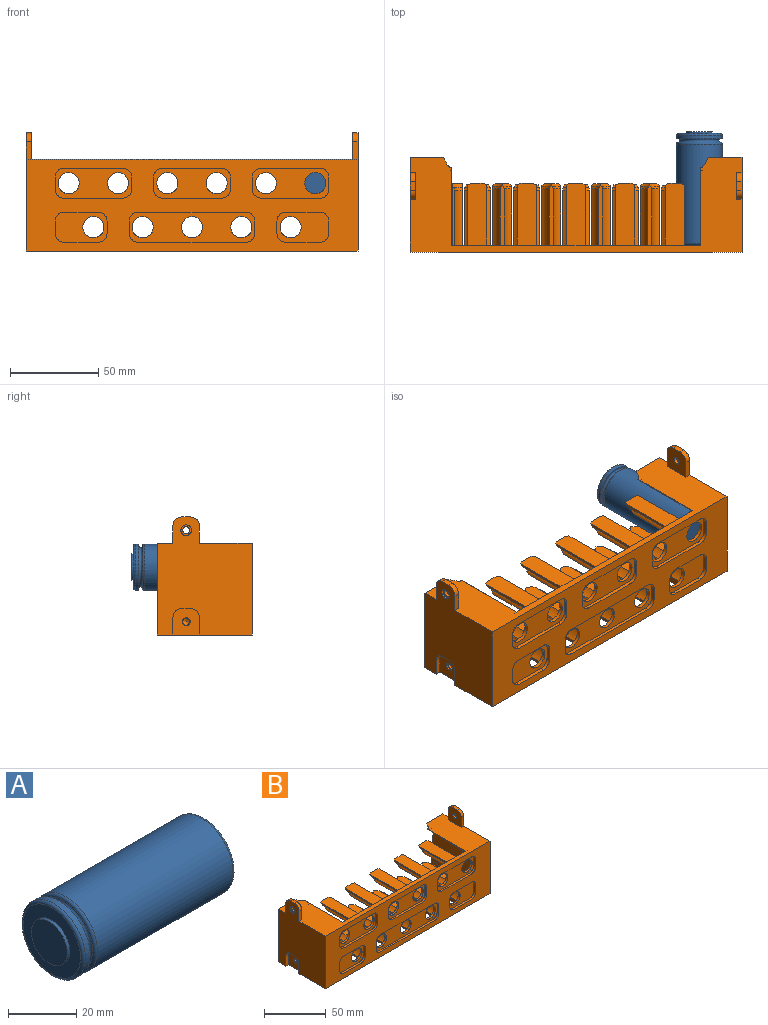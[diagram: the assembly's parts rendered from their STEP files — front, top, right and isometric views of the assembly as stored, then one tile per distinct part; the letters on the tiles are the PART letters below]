
ASSEMBLY  parts=2 mates=1
PART A: 11 faces, bbox 64.4x28.1x28.1 mm
  f0: torus R=11.97mm, axis (-1,0,0), area 223.8mm2, adj f1,f10
  f1: plane 25.95x25.95mm, normal (1,0,0), area 78.4mm2, adj f0,f2
  f2: cylinder r=12.97mm len=25.95mm, axis (-1,0,0), area 163mm2, adj f1,f3
  f3: torus R=11.97mm, axis (-1,0,0), area 124.5mm2, adj f2,f4
  f4: plane 23.95x23.95mm, normal (-1,0,0), area 273.8mm2, adj f3,f5
  f5: cylinder r=7.5mm len=15mm, axis (-1,0,0), area 47.1mm2, adj f4,f6
  f6: plane 15x15mm, normal (-1,0,0), area 176.7mm2, adj f5
  f7: plane 23.95x23.95mm, normal (1,0,0), area 450.5mm2, adj f8
  f8: torus R=11.97mm, axis (-1,0,0), area 124.5mm2, adj f7,f9
  f9: cylinder r=12.97mm len=56.4mm, axis (-1,0,0), area 4598mm2, adj f8,f10
  f10: torus R=11.97mm, axis (-1,0,0), area 124.5mm2, adj f0,f9
PART B: 320 faces, bbox 189.6x55.1x68.2 mm
  f0: plane 10x3mm, normal (0,-1,0), area 30mm2, adj f23,f29,f295,f310
  f1: plane 10x3mm, normal (0,1,0), area 30mm2, adj f23,f29,f295,f311
  f2: plane 10x3mm, normal (0,-1,0), area 30mm2, adj f4,f23,f28,f314
  f3: plane 10x3mm, normal (0,1,0), area 30mm2, adj f4,f23,f28,f315
  f4: plane 15x15mm, normal (1,0,0), area 198.4mm2, adj f2,f3,f23,f290,f306,f314,f315
  f5: plane 188.5x52mm, normal (0,-1,0), area 5493.8mm2, adj f23,f25,f28,f29,f234,f235,f236,f237
  f6: cylinder r=6mm len=12mm, axis (0,1,0), area 75.4mm2, adj f19,f251
  f7: cylinder r=6mm len=12mm, axis (0,1,0), area 75.4mm2, adj f19,f278
  f8: cylinder r=6mm len=12mm, axis (0,1,0), area 75.4mm2, adj f19,f278
  f9: cylinder r=6mm len=12mm, axis (0,1,0), area 75.4mm2, adj f19,f269
  f10: cylinder r=6mm len=12mm, axis (0,1,0), area 75.4mm2, adj f19,f260
  f11: cylinder r=6mm len=12mm, axis (0,1,0), area 75.4mm2, adj f19,f242
  f12: cylinder r=6mm len=12mm, axis (0,1,0), area 75.4mm2, adj f19,f260
  f13: cylinder r=6mm len=12mm, axis (0,1,0), area 75.4mm2, adj f19,f242
  f14: cylinder r=6mm len=12mm, axis (0,1,0), area 75.4mm2, adj f19,f251
  f15: cylinder r=6mm len=12mm, axis (0,1,0), area 75.4mm2, adj f19,f242
  f16: cylinder r=6mm len=12mm, axis (0,1,0), area 75.4mm2, adj f19,f233
  f17: plane 15x12mm, normal (1,0,0), area 180mm2, adj f23,f24,f149,f169
  f18: plane 7.81x4.31mm, normal (0,1,0), area 0.3mm2, adj f141,f145
  f19: plane 166.4x52mm, normal (0,1,0), area 6272.6mm2, adj f6,f7,f8,f9,f10,f11,f12,f13
  f20: plane 15x12mm, normal (-1,0,0), area 180mm2, adj f23,f130,f144,f168
  f21: cylinder r=13.2mm len=15mm, axis (0,-1,0), area 76.9mm2, adj f19,f139,f149,f150
  f22: plane 7.81x4.31mm, normal (0,1,0), area 0.3mm2, adj f139,f151
  f23: plane 188.5x54mm, normal (0,0,-1), area 3135.8mm2, adj f0,f1,f2,f3,f4,f5,f17,f19
  f24: plane 52.04x19.14mm, normal (0,1,0), area 594.4mm2, adj f17,f23,f25,f29,f125,f127,f149,f152
  f25: plane 188.5x54mm, normal (0,0,1), area 3000.9mm2, adj f5,f19,f24,f28,f29,f130,f140,f142
  f26: cone r=2mm half-angle=59deg, axis (0,1,0), area 14.7mm2, adj f27
  f27: cylinder r=2mm len=7.5mm, axis (0,1,0), area 94.2mm2, adj f26,f130
  f28: plane 67x54mm, normal (1,0,0), area 2779.7mm2, adj f2,f3,f5,f23,f25,f130,f287,f288
  f29: plane 67x54mm, normal (-1,0,0), area 2779.7mm2, adj f0,f1,f5,f23,f24,f25,f296,f297
  f30: plane 34.18x2.86mm, normal (-1,0,0), area 90mm2, adj f19,f47,f138,f216
  f31: cylinder r=13.2mm len=31.3mm, axis (0,-1,0), area 169.1mm2, adj f19,f32,f36,f218
  f32: plane 35.13x7.13mm, normal (0,0,1), area 234.3mm2, adj f19,f31,f33,f160,f206,f207,f218,f219
  f33: cylinder r=13.2mm len=31.3mm, axis (0,-1,0), area 169.1mm2, adj f19,f32,f34,f219
  f34: plane 34.35x1.97mm, normal (0.87,0,-0.49), area 74.6mm2, adj f19,f33,f35,f207,f219
  f35: cylinder r=13.2mm len=35mm, axis (0,-1,0), area 469.7mm2, adj f19,f34,f36,f160,f206,f207
  f36: plane 34.35x1.97mm, normal (-0.87,0,-0.49), area 74.6mm2, adj f19,f31,f35,f206,f218
  f37: cylinder r=13.2mm len=32.05mm, axis (0,-1,0), area 266.7mm2, adj f19,f38,f42,f197
  f38: plane 34.03x1.51mm, normal (-1,0,0), area 49.8mm2, adj f19,f37,f39,f171,f197
  f39: plane 35.05x10.82mm, normal (0,0,1), area 375.3mm2, adj f19,f38,f40,f164,f170,f171
  f40: plane 34.03x1.51mm, normal (1,0,0), area 49.8mm2, adj f19,f39,f41,f170,f196
  f41: cylinder r=13.2mm len=32.05mm, axis (0,-1,0), area 266.7mm2, adj f19,f40,f42,f196
  f42: plane 33.97x2.29mm, normal (0,0,-1), area 76.1mm2, adj f19,f37,f41,f170,f171,f196,f197
  f43: plane 34.03x1.51mm, normal (-1,0,0), area 49.8mm2, adj f19,f44,f46,f182,f202
  f44: cylinder r=13.2mm len=32.05mm, axis (0,-1,0), area 266.7mm2, adj f19,f43,f45,f202
  f45: plane 33.97x2.29mm, normal (0,0,1), area 76.1mm2, adj f19,f44,f66,f182,f183,f202,f203
  f46: plane 35.05x10.82mm, normal (0,0,-1), area 375.3mm2, adj f19,f43,f67,f157,f182,f183
  f47: plane 33.22x1.15mm, normal (0,0,1), area 37.2mm2, adj f19,f30,f48,f216,f228
  f48: cylinder r=13.2mm len=31.3mm, axis (0,-1,0), area 260.4mm2, adj f19,f47,f49,f228
  f49: plane 35.05x3.64mm, normal (1,0,0), area 116.9mm2, adj f19,f23,f48,f216,f228
  f50: cylinder r=13.2mm len=31.3mm, axis (0,-1,0), area 169.1mm2, adj f19,f51,f55,f220
  f51: plane 35.13x7.13mm, normal (0,0,1), area 234.3mm2, adj f19,f50,f52,f162,f208,f209,f220,f221
  f52: cylinder r=13.2mm len=31.3mm, axis (0,-1,0), area 169.1mm2, adj f19,f51,f53,f221
  f53: plane 34.35x1.97mm, normal (0.87,0,-0.49), area 74.6mm2, adj f19,f52,f54,f209,f221
  f54: cylinder r=13.2mm len=35mm, axis (0,-1,0), area 469.7mm2, adj f19,f53,f55,f162,f208,f209
  f55: plane 34.35x1.97mm, normal (-0.87,0,-0.49), area 74.6mm2, adj f19,f50,f54,f208,f220
  f56: cylinder r=13.2mm len=32.05mm, axis (0,-1,0), area 266.7mm2, adj f19,f57,f61,f195
  f57: plane 34.03x1.51mm, normal (-1,0,0), area 49.8mm2, adj f19,f56,f58,f173,f195
  f58: plane 35.05x10.82mm, normal (0,0,1), area 375.3mm2, adj f19,f57,f59,f167,f172,f173
  f59: plane 34.03x1.51mm, normal (1,0,0), area 49.8mm2, adj f19,f58,f60,f172,f194
  f60: cylinder r=13.2mm len=32.05mm, axis (0,-1,0), area 266.7mm2, adj f19,f59,f61,f194
  f61: plane 33.97x2.29mm, normal (0,0,-1), area 76.1mm2, adj f19,f56,f60,f172,f173,f194,f195
  f62: plane 34.03x1.51mm, normal (-1,0,0), area 49.8mm2, adj f19,f63,f65,f186,f205
  f63: cylinder r=13.2mm len=32.05mm, axis (0,-1,0), area 266.7mm2, adj f19,f62,f64,f205
  f64: plane 33.97x2.29mm, normal (0,0,1), area 76.1mm2, adj f19,f63,f84,f186,f187,f204,f205
  f65: plane 35.05x10.82mm, normal (0,0,-1), area 375.3mm2, adj f19,f62,f85,f156,f186,f187
  f66: cylinder r=13.2mm len=32.05mm, axis (0,-1,0), area 266.7mm2, adj f19,f45,f67,f203
  f67: plane 34.03x1.51mm, normal (1,0,0), area 49.8mm2, adj f19,f46,f66,f183,f203
  f68: cylinder r=13.2mm len=31.3mm, axis (0,-1,0), area 169.1mm2, adj f19,f69,f73,f222
  f69: plane 35.13x7.13mm, normal (0,0,1), area 234.3mm2, adj f19,f68,f70,f161,f210,f211,f222,f223
  f70: cylinder r=13.2mm len=31.3mm, axis (0,-1,0), area 169.1mm2, adj f19,f69,f71,f223
  f71: plane 34.35x1.97mm, normal (0.87,0,-0.49), area 74.6mm2, adj f19,f70,f72,f211,f223
  f72: cylinder r=13.2mm len=35mm, axis (0,-1,0), area 469.7mm2, adj f19,f71,f73,f161,f210,f211
  f73: plane 34.35x1.97mm, normal (-0.87,0,-0.49), area 74.6mm2, adj f19,f68,f72,f210,f222
  f74: cylinder r=13.2mm len=32.05mm, axis (0,-1,0), area 266.7mm2, adj f19,f75,f79,f193
  f75: plane 34.03x1.51mm, normal (-1,0,0), area 49.8mm2, adj f19,f74,f76,f175,f193
  f76: plane 35.05x10.82mm, normal (0,0,1), area 375.3mm2, adj f19,f75,f77,f166,f174,f175
  f77: plane 34.03x1.51mm, normal (1,0,0), area 49.8mm2, adj f19,f76,f78,f174,f192
  f78: cylinder r=13.2mm len=32.05mm, axis (0,-1,0), area 266.7mm2, adj f19,f77,f79,f192
  f79: plane 33.97x2.29mm, normal (0,0,-1), area 76.1mm2, adj f19,f74,f78,f174,f175,f192,f193
  f80: plane 34.03x1.51mm, normal (-1,0,0), area 49.8mm2, adj f19,f81,f83,f184,f201
  f81: cylinder r=13.2mm len=32.05mm, axis (0,-1,0), area 266.7mm2, adj f19,f80,f82,f201
  f82: plane 33.97x2.29mm, normal (0,0,1), area 76.1mm2, adj f19,f81,f102,f184,f185,f199,f201
  f83: plane 35.05x10.82mm, normal (0,0,-1), area 375.3mm2, adj f19,f80,f103,f155,f184,f185
  f84: cylinder r=13.2mm len=32.05mm, axis (0,-1,0), area 266.7mm2, adj f19,f64,f85,f204
  f85: plane 34.03x1.51mm, normal (1,0,0), area 49.8mm2, adj f19,f65,f84,f187,f204
  f86: cylinder r=13.2mm len=31.3mm, axis (0,-1,0), area 169.1mm2, adj f19,f87,f91,f224
  f87: plane 35.13x7.13mm, normal (0,0,1), area 234.3mm2, adj f19,f86,f88,f159,f212,f213,f224,f225
  f88: cylinder r=13.2mm len=31.3mm, axis (0,-1,0), area 169.1mm2, adj f19,f87,f89,f225
  f89: plane 34.35x1.97mm, normal (0.87,0,-0.49), area 74.6mm2, adj f19,f88,f90,f213,f225
  f90: cylinder r=13.2mm len=35mm, axis (0,-1,0), area 469.7mm2, adj f19,f89,f91,f159,f212,f213
  f91: plane 34.35x1.97mm, normal (-0.87,0,-0.49), area 74.6mm2, adj f19,f86,f90,f212,f224
  f92: cylinder r=13.2mm len=32.05mm, axis (0,-1,0), area 266.7mm2, adj f19,f93,f97,f191
  f93: plane 34.03x1.51mm, normal (-1,0,0), area 49.8mm2, adj f19,f92,f94,f177,f191
  f94: plane 35.05x10.82mm, normal (0,0,1), area 375.3mm2, adj f19,f93,f95,f165,f176,f177
  f95: plane 34.03x1.51mm, normal (1,0,0), area 49.8mm2, adj f19,f94,f96,f176,f190
  f96: cylinder r=13.2mm len=32.05mm, axis (0,-1,0), area 266.7mm2, adj f19,f95,f97,f190
  f97: plane 33.97x2.29mm, normal (0,0,-1), area 76.1mm2, adj f19,f92,f96,f176,f177,f190,f191
  f98: plane 34.03x1.51mm, normal (-1,0,0), area 49.8mm2, adj f19,f99,f101,f180,f200
  f99: cylinder r=13.2mm len=32.05mm, axis (0,-1,0), area 266.7mm2, adj f19,f98,f100,f200
  f100: plane 33.97x2.29mm, normal (0,0,1), area 76.1mm2, adj f19,f99,f120,f180,f181,f198,f200
  f101: plane 35.05x10.82mm, normal (0,0,-1), area 375.3mm2, adj f19,f98,f121,f154,f180,f181
  f102: cylinder r=13.2mm len=32.05mm, axis (0,-1,0), area 266.7mm2, adj f19,f82,f103,f199
  f103: plane 34.03x1.51mm, normal (1,0,0), area 49.8mm2, adj f19,f83,f102,f185,f199
  f104: plane 34.18x2.86mm, normal (1,0,0), area 90mm2, adj f19,f119,f137,f217
  f105: cylinder r=13.2mm len=31.3mm, axis (0,-1,0), area 169.1mm2, adj f19,f106,f110,f226
  f106: plane 35.13x7.13mm, normal (0,0,1), area 234.3mm2, adj f19,f105,f107,f158,f214,f215,f226,f227
  f107: cylinder r=13.2mm len=31.3mm, axis (0,-1,0), area 169.1mm2, adj f19,f106,f108,f227
  f108: plane 33.64x1.97mm, normal (0.87,0,-0.49), area 74.1mm2, adj f19,f107,f109,f214,f227,f230,f232
  f109: cylinder r=13.2mm len=32.58mm, axis (0,-1,0), area 439.1mm2, adj f19,f108,f110,f232
  f110: plane 33.64x1.97mm, normal (-0.87,0,-0.49), area 74.1mm2, adj f19,f105,f109,f215,f226,f231,f232
  f111: cylinder r=13.2mm len=32.05mm, axis (0,-1,0), area 266.7mm2, adj f19,f112,f116,f189
  f112: plane 34.03x1.51mm, normal (-1,0,0), area 49.8mm2, adj f19,f111,f113,f179,f189
  f113: plane 35.05x10.82mm, normal (0,0,1), area 375.3mm2, adj f19,f112,f114,f163,f178,f179
  f114: plane 34.03x1.51mm, normal (1,0,0), area 49.8mm2, adj f19,f113,f115,f178,f188
  f115: cylinder r=13.2mm len=32.05mm, axis (0,-1,0), area 266.7mm2, adj f19,f114,f116,f188
  f116: plane 33.97x2.29mm, normal (0,0,-1), area 76.1mm2, adj f19,f111,f115,f178,f179,f188,f189
  f117: plane 35.05x3.64mm, normal (-1,0,0), area 116.9mm2, adj f19,f23,f118,f217,f229
  f118: cylinder r=13.2mm len=31.3mm, axis (0,-1,0), area 260.4mm2, adj f19,f117,f119,f229
  f119: plane 33.22x1.15mm, normal (0,0,1), area 37.2mm2, adj f19,f104,f118,f217,f229
  f120: cylinder r=13.2mm len=32.05mm, axis (0,-1,0), area 266.7mm2, adj f19,f100,f121,f198
  f121: plane 34.03x1.51mm, normal (1,0,0), area 49.8mm2, adj f19,f101,f120,f181,f198
  f122: cone r=3.52mm half-angle=59deg, axis (0,1,0), area 45.5mm2, adj f123
  f123: cylinder r=3.52mm len=7.05mm, axis (0,1,0), area 135.1mm2, adj f122,f124
  f124: plane 7.5x7.5mm, normal (0,1,0), area 5.1mm2, adj f123,f125
  f125: cylinder r=3.75mm len=7.5mm, axis (0,1,0), area 23.6mm2, adj f24,f124
  f126: cone r=2mm half-angle=59deg, axis (0,1,0), area 14.7mm2, adj f127
  f127: cylinder r=2mm len=7.5mm, axis (0,1,0), area 94.2mm2, adj f24,f126
  f128: cylinder r=13.2mm len=15mm, axis (0,-1,0), area 76.9mm2, adj f19,f129,f141,f144
  f129: cone r=13.2mm half-angle=8deg, axis (0,1,0), area 0mm2, adj f128,f143,f146
  f130: plane 52.03x19.14mm, normal (0,1,0), area 594.4mm2, adj f20,f23,f25,f27,f28,f134,f144,f147
  f131: cone r=3.52mm half-angle=59deg, axis (0,1,0), area 45.5mm2, adj f132
  f132: cylinder r=3.52mm len=7.05mm, axis (0,1,0), area 135.1mm2, adj f131,f133
  f133: plane 7.5x7.5mm, normal (0,1,0), area 5.1mm2, adj f132,f134
  f134: cylinder r=3.75mm len=7.5mm, axis (0,1,0), area 23.6mm2, adj f130,f133
  f135: extruded ~35x7.31mm, area 306.1mm2, adj f19,f137,f144,f168
  f136: extruded ~35x7.31mm, area 306.1mm2, adj f19,f138,f149,f169
  f137: cylinder r=4mm len=35mm, axis (0,-1,0), area 313mm2, adj f19,f104,f135,f168,f217
  f138: cylinder r=4mm len=35mm, axis (0,-1,0), area 313mm2, adj f19,f30,f136,f169,f216
  f139: cylinder r=12.55mm len=15mm, axis (0,-1,0), area 226.5mm2, adj f19,f21,f22,f140,f150,f151
  f140: plane 43.78x0.46mm, normal (1,0,0), area 19mm2, adj f19,f25,f139,f151,f152,f153
  f141: cylinder r=12.55mm len=15mm, axis (0,-1,0), area 226.5mm2, adj f18,f19,f128,f142,f145,f146
  f142: plane 43.78x0.46mm, normal (-1,0,0), area 19mm2, adj f19,f25,f141,f145,f147,f148
  f143: plane 0x0mm, normal (0,0,-1), area 0mm2, adj f129
  f144: plane 51.1x32.4mm, normal (-1,0,0.08), area 1361.7mm2, adj f19,f20,f128,f130,f135,f145,f147,f148
  f145: extruded ~22x13.04mm, area 445.3mm2, adj f18,f141,f142,f144,f146,f148
  f146: plane 9.03x3.52mm, normal (0,-1,0), area 0.1mm2, adj f129,f141,f145
  f147: bspline ~13.9x13.28mm, area 122.4mm2, adj f25,f130,f142,f144,f148
  f148: bspline ~13.32x13mm, area 102.5mm2, adj f142,f144,f145,f147
  f149: plane 51.1x32.4mm, normal (1,0,0.08), area 1361.7mm2, adj f17,f19,f21,f24,f136,f151,f152,f153
  f150: plane 9.04x3.52mm, normal (0,-1,0), area 0.1mm2, adj f21,f139,f151
  f151: extruded ~22x13.04mm, area 445.3mm2, adj f22,f139,f140,f149,f150,f153
  f152: bspline ~13.9x13.28mm, area 122.4mm2, adj f24,f25,f140,f149,f153
  f153: bspline ~13.31x12.98mm, area 102.5mm2, adj f140,f149,f151,f152
  f154: plane 7.67x5.21mm, normal (0,1,0), area 17mm2, adj f101,f180,f181
  f155: plane 7.67x5.21mm, normal (0,1,0), area 17mm2, adj f83,f184,f185
  f156: plane 7.67x5.21mm, normal (0,1,0), area 17mm2, adj f65,f186,f187
  f157: plane 7.67x5.21mm, normal (0,1,0), area 17mm2, adj f46,f182,f183
  f158: plane 4.44x2.97mm, normal (0,1,0), area 5.6mm2, adj f106,f214,f215,f232
  f159: plane 7.24x4.31mm, normal (0,1,0), area 11.4mm2, adj f87,f90,f212,f213
  f160: plane 7.24x4.31mm, normal (0,1,0), area 11.4mm2, adj f32,f35,f206,f207
  f161: plane 7.24x4.31mm, normal (0,1,0), area 11.4mm2, adj f69,f72,f210,f211
  f162: plane 7.24x4.31mm, normal (0,1,0), area 11.4mm2, adj f51,f54,f208,f209
  f163: plane 7.67x5.21mm, normal (0,1,0), area 17mm2, adj f113,f178,f179
  f164: plane 7.67x5.21mm, normal (0,1,0), area 17mm2, adj f39,f170,f171
  f165: plane 7.67x5.21mm, normal (0,1,0), area 17mm2, adj f94,f176,f177
  f166: plane 7.67x5.21mm, normal (0,1,0), area 17mm2, adj f76,f174,f175
  f167: plane 7.67x5.21mm, normal (0,1,0), area 17mm2, adj f58,f172,f173
  f168: plane 16.23x12mm, normal (0,1,0), area 74.4mm2, adj f20,f23,f135,f137,f217
  f169: plane 16.23x12mm, normal (0,1,0), area 74.4mm2, adj f17,f23,f136,f138,f216
  f170: cone r=15.35mm half-angle=45deg, axis (0,1,0), area 20mm2, adj f39,f40,f42,f164,f171,f196
  f171: cone r=15.35mm half-angle=45deg, axis (0,1,0), area 20mm2, adj f38,f39,f42,f164,f170,f197
  f172: cone r=15.35mm half-angle=45deg, axis (0,1,0), area 20mm2, adj f58,f59,f61,f167,f173,f194
  f173: cone r=15.35mm half-angle=45deg, axis (0,1,0), area 20mm2, adj f57,f58,f61,f167,f172,f195
  f174: cone r=15.35mm half-angle=45deg, axis (0,1,0), area 20mm2, adj f76,f77,f79,f166,f175,f192
  f175: cone r=15.35mm half-angle=45deg, axis (0,1,0), area 20mm2, adj f75,f76,f79,f166,f174,f193
  f176: cone r=15.35mm half-angle=45deg, axis (0,1,0), area 20mm2, adj f94,f95,f97,f165,f177,f190
  f177: cone r=15.35mm half-angle=45deg, axis (0,1,0), area 20mm2, adj f93,f94,f97,f165,f176,f191
  f178: cone r=15.35mm half-angle=45deg, axis (0,1,0), area 20mm2, adj f113,f114,f116,f163,f179,f188
  f179: cone r=15.35mm half-angle=45deg, axis (0,1,0), area 20mm2, adj f112,f113,f116,f163,f178,f189
  f180: cone r=15.35mm half-angle=45deg, axis (0,1,0), area 20mm2, adj f98,f100,f101,f154,f181,f200
  f181: cone r=15.35mm half-angle=45deg, axis (0,1,0), area 20mm2, adj f100,f101,f121,f154,f180,f198
  f182: cone r=15.35mm half-angle=45deg, axis (0,1,0), area 20mm2, adj f43,f45,f46,f157,f183,f202
  f183: cone r=15.35mm half-angle=45deg, axis (0,1,0), area 20mm2, adj f45,f46,f67,f157,f182,f203
  f184: cone r=15.35mm half-angle=45deg, axis (0,1,0), area 20mm2, adj f80,f82,f83,f155,f185,f201
  f185: cone r=15.35mm half-angle=45deg, axis (0,1,0), area 20mm2, adj f82,f83,f103,f155,f184,f199
  f186: cone r=15.35mm half-angle=45deg, axis (0,1,0), area 20mm2, adj f62,f64,f65,f156,f187,f205
  f187: cone r=15.35mm half-angle=45deg, axis (0,1,0), area 20mm2, adj f64,f65,f85,f156,f186,f204
  f188: cone r=13.2mm half-angle=22.5deg, axis (0,1,0), area 13mm2, adj f114,f115,f116,f178
  f189: cone r=13.2mm half-angle=22.5deg, axis (0,1,0), area 13mm2, adj f111,f112,f116,f179
  f190: cone r=13.2mm half-angle=22.5deg, axis (0,1,0), area 13mm2, adj f95,f96,f97,f176
  f191: cone r=13.2mm half-angle=22.5deg, axis (0,1,0), area 13mm2, adj f92,f93,f97,f177
  f192: cone r=13.2mm half-angle=22.5deg, axis (0,1,0), area 13mm2, adj f77,f78,f79,f174
  f193: cone r=13.2mm half-angle=22.5deg, axis (0,1,0), area 13mm2, adj f74,f75,f79,f175
  f194: cone r=13.2mm half-angle=22.5deg, axis (0,1,0), area 13mm2, adj f59,f60,f61,f172
  f195: cone r=13.2mm half-angle=22.5deg, axis (0,1,0), area 13mm2, adj f56,f57,f61,f173
  f196: cone r=13.2mm half-angle=22.5deg, axis (0,1,0), area 13mm2, adj f40,f41,f42,f170
  f197: cone r=13.2mm half-angle=22.5deg, axis (0,1,0), area 13mm2, adj f37,f38,f42,f171
  f198: cone r=13.2mm half-angle=22.5deg, axis (0,1,0), area 13mm2, adj f100,f120,f121,f181
  f199: cone r=13.2mm half-angle=22.5deg, axis (0,1,0), area 13mm2, adj f82,f102,f103,f185
  f200: cone r=13.2mm half-angle=22.5deg, axis (0,1,0), area 13mm2, adj f98,f99,f100,f180
  f201: cone r=13.2mm half-angle=22.5deg, axis (0,1,0), area 13mm2, adj f80,f81,f82,f184
  f202: cone r=13.2mm half-angle=22.5deg, axis (0,1,0), area 13mm2, adj f43,f44,f45,f182
  f203: cone r=13.2mm half-angle=22.5deg, axis (0,1,0), area 13mm2, adj f45,f66,f67,f183
  f204: cone r=13.2mm half-angle=22.5deg, axis (0,1,0), area 13mm2, adj f64,f84,f85,f187
  f205: cone r=13.2mm half-angle=22.5deg, axis (0,1,0), area 13mm2, adj f62,f63,f64,f186
  f206: cone r=16.1mm half-angle=45deg, axis (0,1,0), area 22.8mm2, adj f32,f35,f36,f160,f218
  f207: cone r=16.1mm half-angle=45deg, axis (0,1,0), area 22.8mm2, adj f32,f34,f35,f160,f219
  f208: cone r=16.1mm half-angle=45deg, axis (0,1,0), area 22.8mm2, adj f51,f54,f55,f162,f220
  f209: cone r=16.1mm half-angle=45deg, axis (0,1,0), area 22.8mm2, adj f51,f53,f54,f162,f221
  f210: cone r=16.1mm half-angle=45deg, axis (0,1,0), area 22.8mm2, adj f69,f72,f73,f161,f222
  f211: cone r=16.1mm half-angle=45deg, axis (0,1,0), area 22.8mm2, adj f69,f71,f72,f161,f223
  f212: cone r=16.1mm half-angle=45deg, axis (0,1,0), area 22.8mm2, adj f87,f90,f91,f159,f224
  f213: cone r=16.1mm half-angle=45deg, axis (0,1,0), area 22.8mm2, adj f87,f89,f90,f159,f225
  f214: cone r=16.1mm half-angle=45deg, axis (0,1,0), area 18.8mm2, adj f106,f108,f158,f227,f230,f232
  f215: cone r=16.1mm half-angle=45deg, axis (0,1,0), area 18.8mm2, adj f106,f110,f158,f226,f231,f232
  f216: cone r=16.1mm half-angle=45deg, axis (0,1,0), area 30.1mm2, adj f23,f30,f47,f49,f138,f169,f228
  f217: cone r=16.1mm half-angle=45deg, axis (0,1,0), area 30.1mm2, adj f23,f104,f117,f119,f137,f168,f229
  f218: cone r=13.2mm half-angle=22.5deg, axis (0,1,0), area 8.5mm2, adj f31,f32,f36,f206
  f219: cone r=13.2mm half-angle=22.5deg, axis (0,1,0), area 8.5mm2, adj f32,f33,f34,f207
  f220: cone r=13.2mm half-angle=22.5deg, axis (0,1,0), area 8.5mm2, adj f50,f51,f55,f208
  f221: cone r=13.2mm half-angle=22.5deg, axis (0,1,0), area 8.5mm2, adj f51,f52,f53,f209
  f222: cone r=13.2mm half-angle=22.5deg, axis (0,1,0), area 8.5mm2, adj f68,f69,f73,f210
  f223: cone r=13.2mm half-angle=22.5deg, axis (0,1,0), area 8.5mm2, adj f69,f70,f71,f211
  f224: cone r=13.2mm half-angle=22.5deg, axis (0,1,0), area 8.5mm2, adj f86,f87,f91,f212
  f225: cone r=13.2mm half-angle=22.5deg, axis (0,1,0), area 8.5mm2, adj f87,f88,f89,f213
  f226: cone r=13.2mm half-angle=22.5deg, axis (0,1,0), area 8.5mm2, adj f105,f106,f110,f215
  f227: cone r=13.2mm half-angle=22.5deg, axis (0,1,0), area 8.5mm2, adj f106,f107,f108,f214
  f228: cone r=13.2mm half-angle=22.5deg, axis (0,1,0), area 13mm2, adj f47,f48,f49,f216
  f229: cone r=13.2mm half-angle=22.5deg, axis (0,1,0), area 13mm2, adj f117,f118,f119,f217
  f230: bspline ~4.87x2.24mm, area 0.5mm2, adj f108,f214,f232
  f231: bspline ~2.84x1.42mm, area 0.5mm2, adj f110,f215,f232
  f232: cone r=13.2mm half-angle=22.5deg, axis (0,1,0), area 27.8mm2, adj f108,f109,f110,f158,f214,f215,f230,f231
  f233: plane 29.5x17mm, normal (0,-1,0), area 366.9mm2, adj f16,f234,f235,f236,f237,f238,f239,f240
  f234: plane 7x2mm, normal (1,0,0), area 14mm2, adj f5,f233,f235,f241
  f235: cylinder r=5mm len=5mm, axis (0,-1,0), area 15.7mm2, adj f5,f233,f234,f236
  f236: plane 19.5x2mm, normal (0,0,1), area 39mm2, adj f5,f233,f235,f237
  f237: cylinder r=5mm len=5mm, axis (0,-1,0), area 15.7mm2, adj f5,f233,f236,f238
  f238: plane 7x2mm, normal (-1,0,0), area 14mm2, adj f5,f233,f237,f239
  f239: cylinder r=5mm len=5mm, axis (0,-1,0), area 15.7mm2, adj f5,f233,f238,f240
  f240: plane 19.5x2mm, normal (0,0,-1), area 39mm2, adj f5,f233,f239,f241
  f241: cylinder r=5mm len=5mm, axis (0,-1,0), area 15.7mm2, adj f5,f233,f234,f240
  f242: plane 71.5x17mm, normal (0,-1,0), area 854.7mm2, adj f11,f13,f15,f243,f244,f245,f246,f247
  f243: plane 61.5x2mm, normal (0,0,-1), area 123mm2, adj f5,f242,f244,f250
  f244: cylinder r=5mm len=5mm, axis (0,-1,0), area 15.7mm2, adj f5,f242,f243,f245
  f245: plane 7x2mm, normal (1,0,0), area 14mm2, adj f5,f242,f244,f246
  f246: cylinder r=5mm len=5mm, axis (0,-1,0), area 15.7mm2, adj f5,f242,f245,f247
  f247: plane 61.5x2mm, normal (0,0,1), area 123mm2, adj f5,f242,f246,f248
  f248: cylinder r=5mm len=5mm, axis (0,-1,0), area 15.7mm2, adj f5,f242,f247,f249
  f249: plane 7x2mm, normal (-1,0,0), area 14mm2, adj f5,f242,f248,f250
  f250: cylinder r=5mm len=5mm, axis (0,-1,0), area 15.7mm2, adj f5,f242,f243,f249
  f251: plane 43.5x17mm, normal (0,-1,0), area 491.8mm2, adj f6,f14,f252,f253,f254,f255,f256,f257
  f252: plane 7x2mm, normal (-1,0,0), area 14mm2, adj f5,f251,f253,f259
  f253: cylinder r=5mm len=5mm, axis (0,-1,0), area 15.7mm2, adj f5,f251,f252,f254
  f254: plane 33.5x2mm, normal (0,0,-1), area 67mm2, adj f5,f251,f253,f255
  f255: cylinder r=5mm len=5mm, axis (0,-1,0), area 15.7mm2, adj f5,f251,f254,f256
  f256: plane 7x2mm, normal (1,0,0), area 14mm2, adj f5,f251,f255,f257
  f257: cylinder r=5mm len=5mm, axis (0,-1,0), area 15.7mm2, adj f5,f251,f256,f258
  f258: plane 33.5x2mm, normal (0,0,1), area 67mm2, adj f5,f251,f257,f259
  f259: cylinder r=5mm len=5mm, axis (0,-1,0), area 15.7mm2, adj f5,f251,f252,f258
  f260: plane 43.5x17mm, normal (0,-1,0), area 491.8mm2, adj f10,f12,f261,f262,f263,f264,f265,f266
  f261: plane 33.5x2mm, normal (0,0,-1), area 67mm2, adj f5,f260,f262,f268
  f262: cylinder r=5mm len=5mm, axis (0,-1,0), area 15.7mm2, adj f5,f260,f261,f263
  f263: plane 7x2mm, normal (1,0,0), area 14mm2, adj f5,f260,f262,f264
  f264: cylinder r=5mm len=5mm, axis (0,-1,0), area 15.7mm2, adj f5,f260,f263,f265
  f265: plane 33.5x2mm, normal (0,0,1), area 67mm2, adj f5,f260,f264,f266
  f266: cylinder r=5mm len=5mm, axis (0,-1,0), area 15.7mm2, adj f5,f260,f265,f267
  f267: plane 7x2mm, normal (-1,0,0), area 14mm2, adj f5,f260,f266,f268
  f268: cylinder r=5mm len=5mm, axis (0,-1,0), area 15.7mm2, adj f5,f260,f261,f267
  f269: plane 29.5x17mm, normal (0,-1,0), area 366.9mm2, adj f9,f270,f271,f272,f273,f274,f275,f276
  f270: plane 7x2mm, normal (-1,0,0), area 14mm2, adj f5,f269,f271,f277
  f271: cylinder r=5mm len=5mm, axis (0,-1,0), area 15.7mm2, adj f5,f269,f270,f272
  f272: plane 19.5x2mm, normal (0,0,-1), area 39mm2, adj f5,f269,f271,f273
  f273: cylinder r=5mm len=5mm, axis (0,-1,0), area 15.7mm2, adj f5,f269,f272,f274
  f274: plane 7x2mm, normal (1,0,0), area 14mm2, adj f5,f269,f273,f275
  f275: cylinder r=5mm len=5mm, axis (0,-1,0), area 15.7mm2, adj f5,f269,f274,f276
  f276: plane 19.5x2mm, normal (0,0,1), area 39mm2, adj f5,f269,f275,f277
  f277: cylinder r=5mm len=5mm, axis (0,-1,0), area 15.7mm2, adj f5,f269,f270,f276
  f278: plane 43.5x17mm, normal (0,-1,0), area 491.8mm2, adj f7,f8,f279,f280,f281,f282,f283,f284
  f279: plane 7x2mm, normal (-1,0,0), area 14mm2, adj f5,f278,f280,f286
  f280: cylinder r=5mm len=5mm, axis (0,-1,0), area 15.7mm2, adj f5,f278,f279,f281
  f281: plane 33.5x2mm, normal (0,0,-1), area 67mm2, adj f5,f278,f280,f282
  f282: cylinder r=5mm len=5mm, axis (0,-1,0), area 15.7mm2, adj f5,f278,f281,f283
  f283: plane 7x2mm, normal (1,0,0), area 14mm2, adj f5,f278,f282,f284
  f284: cylinder r=5mm len=5mm, axis (0,-1,0), area 15.7mm2, adj f5,f278,f283,f285
  f285: plane 33.5x2mm, normal (0,0,1), area 67mm2, adj f5,f278,f284,f286
  f286: cylinder r=5mm len=5mm, axis (0,-1,0), area 15.7mm2, adj f5,f278,f279,f285
  f287: plane 10x3mm, normal (0,-1,0), area 30mm2, adj f25,f28,f289,f313
  f288: plane 10x3mm, normal (0,1,0), area 30mm2, adj f25,f28,f289,f312
  f289: plane 15x15mm, normal (-1,0,0), area 201.7mm2, adj f25,f287,f288,f291,f292,f312,f313
  f290: plane 5x3mm, normal (0,0,-1), area 15mm2, adj f4,f28,f314,f315
  f291: plane 5x3mm, normal (0,0,1), area 15mm2, adj f28,f289,f312,f313
  f292: cylinder r=2mm len=4mm, axis (1,0,0), area 25.1mm2, adj f289,f293
  f293: plane 6x6mm, normal (1,0,0), area 15.7mm2, adj f292,f294
  f294: cylinder r=3mm len=6mm, axis (1,0,0), area 18.8mm2, adj f28,f293
  f295: plane 15x15mm, normal (-1,0,0), area 198.4mm2, adj f0,f1,f23,f299,f310,f311,f318
  f296: plane 10x3mm, normal (0,1,0), area 30mm2, adj f25,f29,f298,f309
  f297: plane 10x3mm, normal (0,-1,0), area 30mm2, adj f25,f29,f298,f308
  f298: plane 15x15mm, normal (1,0,0), area 201.7mm2, adj f25,f296,f297,f300,f301,f308,f309
  f299: plane 5x3mm, normal (0,0,-1), area 15mm2, adj f29,f295,f310,f311
  f300: plane 5x3mm, normal (0,0,1), area 15mm2, adj f29,f298,f308,f309
  f301: cylinder r=2mm len=4mm, axis (-1,0,0), area 25.1mm2, adj f298,f302
  f302: plane 6x6mm, normal (-1,0,0), area 15.7mm2, adj f301,f303
  f303: cylinder r=3mm len=6mm, axis (-1,0,0), area 18.8mm2, adj f29,f302
  f304: cylinder r=2mm len=4mm, axis (1,0,0), area 50.3mm2, adj f305,f307
  f305: plane 4.5x4.5mm, normal (1,0,0), area 3.3mm2, adj f304,f306
  f306: cylinder r=2.25mm len=4.5mm, axis (1,0,0), area 14.1mm2, adj f4,f305
  f307: cone r=0mm half-angle=59deg, axis (1,0,0), area 14.7mm2, adj f304
  f308: cylinder r=5mm len=5mm, axis (-1,0,0), area 23.6mm2, adj f29,f297,f298,f300
  f309: cylinder r=5mm len=5mm, axis (1,0,0), area 23.6mm2, adj f29,f296,f298,f300
  f310: cylinder r=5mm len=5mm, axis (-1,0,0), area 23.6mm2, adj f0,f29,f295,f299
  f311: cylinder r=5mm len=5mm, axis (1,0,0), area 23.6mm2, adj f1,f29,f295,f299
  f312: cylinder r=5mm len=5mm, axis (-1,0,0), area 23.6mm2, adj f28,f288,f289,f291
  f313: cylinder r=5mm len=5mm, axis (1,0,0), area 23.6mm2, adj f28,f287,f289,f291
  f314: cylinder r=5mm len=5mm, axis (1,0,0), area 23.6mm2, adj f2,f4,f28,f290
  f315: cylinder r=5mm len=5mm, axis (-1,0,0), area 23.6mm2, adj f3,f4,f28,f290
  f316: cylinder r=2mm len=4mm, axis (-1,0,0), area 50.3mm2, adj f317,f319
  f317: plane 4.5x4.5mm, normal (-1,0,0), area 3.3mm2, adj f316,f318
  f318: cylinder r=2.25mm len=4.5mm, axis (-1,0,0), area 14.1mm2, adj f295,f317
  f319: cone r=0mm half-angle=59deg, axis (-1,0,0), area 14.7mm2, adj f316
PLACE A rot(axis=(0.58,-0.58,-0.58),120deg) t=(12.83,8.92,39.43)mm
PLACE B t=(-1.17,-39.39,26.93)mm
MATE fastened A.f0 <-> B.f6  axis (0,-1,0) through (12.83,-35.39,39.43)mm
